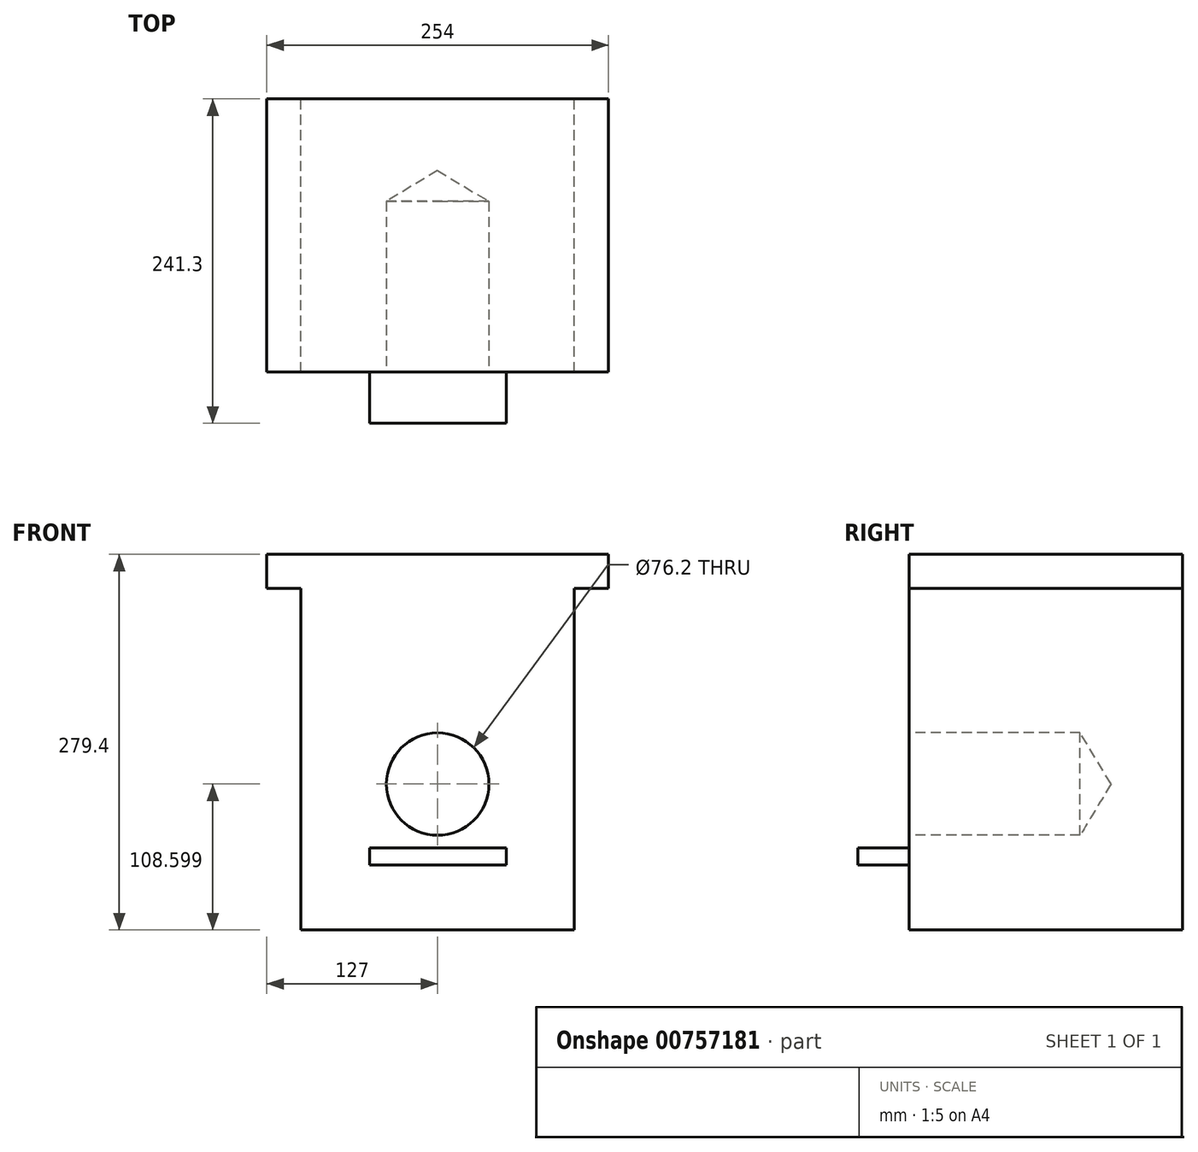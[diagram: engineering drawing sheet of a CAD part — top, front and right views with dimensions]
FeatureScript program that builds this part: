
annotation { "Feature Type Name" : "Feature", "Feature Type Description" : "" }
export const myFeature = defineFeature(function(context is Context, id is Id, definition is map)
    precondition{}
    {
        {
            var Q0;
            Q0=qCreatedBy(makeId("Top.planeOp"),FACE);
            var sketch = newSketch(context, id + "F0", { "sketchPlane" : qUnion([Q0])});
            skLineSegment(sketch, "E0", {"start": v(0, 0) * mm, "end": v(-203.2, 0) * mm});
            skLineSegment(sketch, "E1", {"start": v(0, 0) * mm, "end": v(0, 203.2) * mm});
            skLineSegment(sketch, "E2", {"start": v(-203.2, 0) * mm, "end": v(-203.2, 203.2) * mm});
            skLineSegment(sketch, "E3", {"start": v(0, 203.2) * mm, "end": v(-203.2, 203.2) * mm});
            skSolve(sketch);
        }
        {
            var Q0;
            Q0 = qSketchRegion(id + "F0", true);
            extrude(context, id + "F1", {"entities" : qUnion([Q0]), "depth" : 254 * mm, "offsetDistance" : 25.4 * mm});
        }
        {
            var Q0;
            Q0=makeQuery(id+"F1.opExtrude","SWEPT_FACE",FACE,{"disambiguationData":[OSD([sQuery(id+"F0.wireOp",EDGE,"E0")])]});
            var sketch = newSketch(context, id + "F2", { "sketchPlane" : qUnion([Q0])});
            skCircle(sketch, "E4", {"center": v(-101.6, 108.6) * mm, "radius": 44.45 * mm});
            skSolve(sketch);
        }
        {
            var Q0;
            Q0=makeQuery(id+"F1.opExtrude","CAP_FACE",FACE,{"disambiguationData":[OSD([sQuery(id+"F0.wireOp",EDGE,"E0"),sQuery(id+"F0.wireOp",EDGE,"E1"),sQuery(id+"F0.wireOp",EDGE,"E2"),sQuery(id+"F0.wireOp",EDGE,"E3")])],"isStart":false});
            var sketch = newSketch(context, id + "F3", { "sketchPlane" : qUnion([Q0])});
            skLineSegment(sketch, "E5", {"start": v(-203.2, 0) * mm, "end": v(-228.6, 0) * mm});
            skLineSegment(sketch, "E6", {"start": v(-203.2, 203.2) * mm, "end": v(-228.6, 203.2) * mm});
            skLineSegment(sketch, "E7", {"start": v(-228.6, 203.2) * mm, "end": v(-228.6, 0) * mm});
            skLineSegment(sketch, "E8", {"start": v(0, 203.2) * mm, "end": v(25.4, 203.2) * mm});
            skLineSegment(sketch, "E9", {"start": v(25.4, 203.2) * mm, "end": v(25.4, 0) * mm});
            skLineSegment(sketch, "E10", {"start": v(25.4, 0) * mm, "end": v(0, 0) * mm});
            skSolve(sketch);
        }
        {
            var Q0;
            Q0=makeQuery(id+"F3.imprint","IMPRINT",FACE,{"disambiguationData":[TD([[makeQuery(id+"F3.imprint","IMPRINT",EDGE,{"derivedFrom":sQuery(id+"F3.wireOp",EDGE,"E5")}),-1.0]])]});
            var Q1;
            Q1=makeQuery(id+"F3.imprint","IMPRINT",FACE,{"disambiguationData":[TD([[makeQuery(id+"F3.imprint","IMPRINT",EDGE,{"derivedFrom":sQuery(id+"F3.wireOp",EDGE,"E8")}),-1.0]])]});
            var Q2;
            Q2=makeQuery(id+"F3.imprint","IMPRINT",FACE,{"disambiguationData":[TD([[makeQuery(id+"F3.imprint","IMPRINT",EDGE,{"derivedFrom":makeQuery(id+"F1.opExtrude","CAP_EDGE",EDGE,{"disambiguationData":[OSD([sQuery(id+"F0.wireOp",EDGE,"E0")])],"isStart":false})}),-1.0]])]});
            extrude(context, id + "F4", {"entities" : qUnion([Q0, Q1, Q2]), "operationType" : NewBodyOperationType.ADD, "depth" : 25.4 * mm, "offsetDistance" : 25.4 * mm});
        }
        {
            var Q0;
            Q0=sQuery(id+"F2.wireOp",VERTEX,"E4.center");
            var Q1;
            Q1=makeQuery(id+"F1.opExtrude","SWEPT_BODY",BODY,{"disambiguationData":[OSD([sQuery(id+"F0.wireOp",EDGE,"E0"),sQuery(id+"F0.wireOp",EDGE,"E1"),sQuery(id+"F0.wireOp",EDGE,"E2"),sQuery(id+"F0.wireOp",EDGE,"E3")])]});
            hole(context, id + "F5", {"style" : HoleStyle.SIMPLE, "endStyle" : HoleEndStyle.BLIND, "holeDiameter" : 76.2 * mm, "majorDiameter" : 6.35 * mm, "holeDepth" : 127 * mm, "isTappedThrough" : true, "tappedDepth" : 12.7 * mm, "tapClearance" : 3, "locations" : qUnion([Q0]), "scope" : qUnion([Q1])});
        }
        {
            var Q0;
            {var subQ0=sQuery(id+"F0.wireOp",EDGE,"E0");Q0=makeQuery(id+"F4.boolean.opBoolean","MERGE",FACE,{"derivedFrom":[makeQuery(id+"F1.opExtrude","SWEPT_FACE",FACE,{"disambiguationData":[OSD([subQ0])]}),makeQuery(id+"F4.opExtrude","SWEPT_FACE",FACE,{"disambiguationData":[OSD([subQ0,sQuery(id+"F3.wireOp",EDGE,"E5"),sQuery(id+"F3.wireOp",EDGE,"E10")])]})]});}
            var sketch = newSketch(context, id + "F6", { "sketchPlane" : qUnion([Q0])});
            skLineSegment(sketch, "E11", {"start": v(-152.25, 48.4) * mm, "end": v(-50.65, 48.4) * mm});
            skLineSegment(sketch, "E12", {"start": v(-152.25, 48.4) * mm, "end": v(-152.25, 61.1) * mm});
            skLineSegment(sketch, "E13", {"start": v(-152.25, 61.1) * mm, "end": v(-50.65, 61.1) * mm});
            skLineSegment(sketch, "E14", {"start": v(-50.65, 61.1) * mm, "end": v(-50.65, 48.4) * mm});
            skSolve(sketch);
        }
        {
            var Q0;
            Q0 = qSketchRegion(id + "F6", true);
            extrude(context, id + "F7", {"entities" : qUnion([Q0]), "operationType" : NewBodyOperationType.ADD, "depth" : 38.1 * mm, "offsetDistance" : 25.4 * mm});
        }
    });
